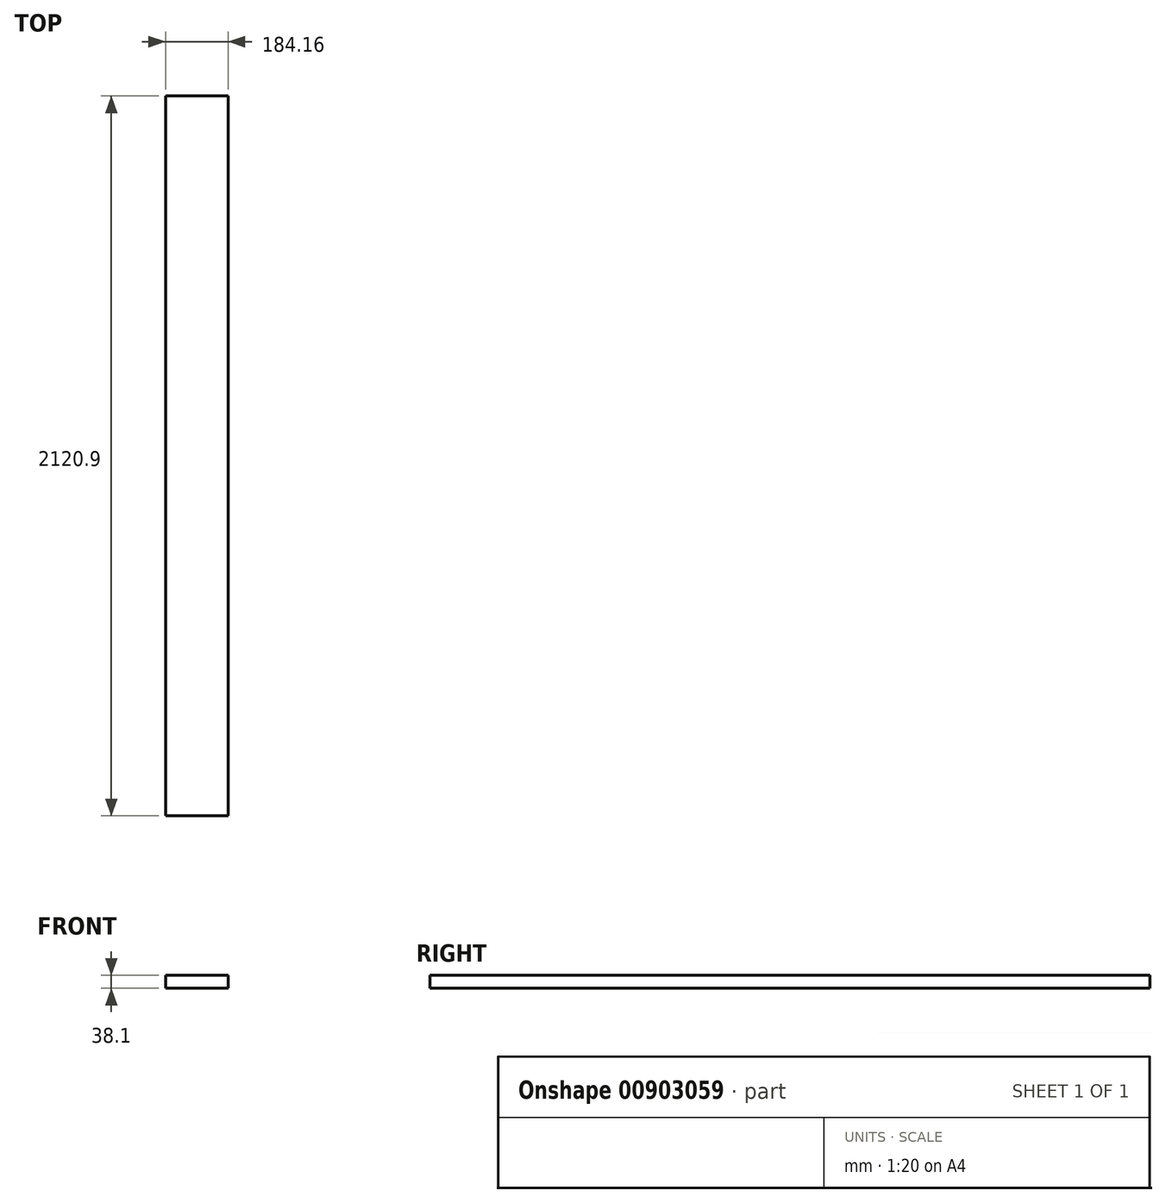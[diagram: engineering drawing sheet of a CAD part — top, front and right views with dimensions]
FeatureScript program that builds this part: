
annotation { "Feature Type Name" : "Feature", "Feature Type Description" : "" }
export const myFeature = defineFeature(function(context is Context, id is Id, definition is map)
    precondition{}
    {
        {
            var Q0;
            Q0=qCreatedBy(makeId("Front.planeOp"),FACE);
            var sketch = newSketch(context, id + "F0", { "sketchPlane" : qUnion([Q0])});
            skLineSegment(sketch, "E0.bottom", {"start": v(92.08, 19.05) * mm, "end": v(-92.08, 19.05) * mm});
            skLineSegment(sketch, "E0.top", {"start": v(92.08, -19.05) * mm, "end": v(-92.08, -19.05) * mm});
            skLineSegment(sketch, "E0.left", {"start": v(92.08, 19.05) * mm, "end": v(92.08, -19.05) * mm});
            skLineSegment(sketch, "E0.right", {"start": v(-92.08, 19.05) * mm, "end": v(-92.08, -19.05) * mm});
            skPoint(sketch, "E0.middle", {"position": v(0, 0) * mm});
            skSolve(sketch);
        }
        {
            var Q0;
            Q0 = qSketchRegion(id + "F0", true);
            extrude(context, id + "F1", {"entities" : qUnion([Q0]), "depth" : 2120.9 * mm, "offsetDistance" : 25.4 * mm});
        }
    });
